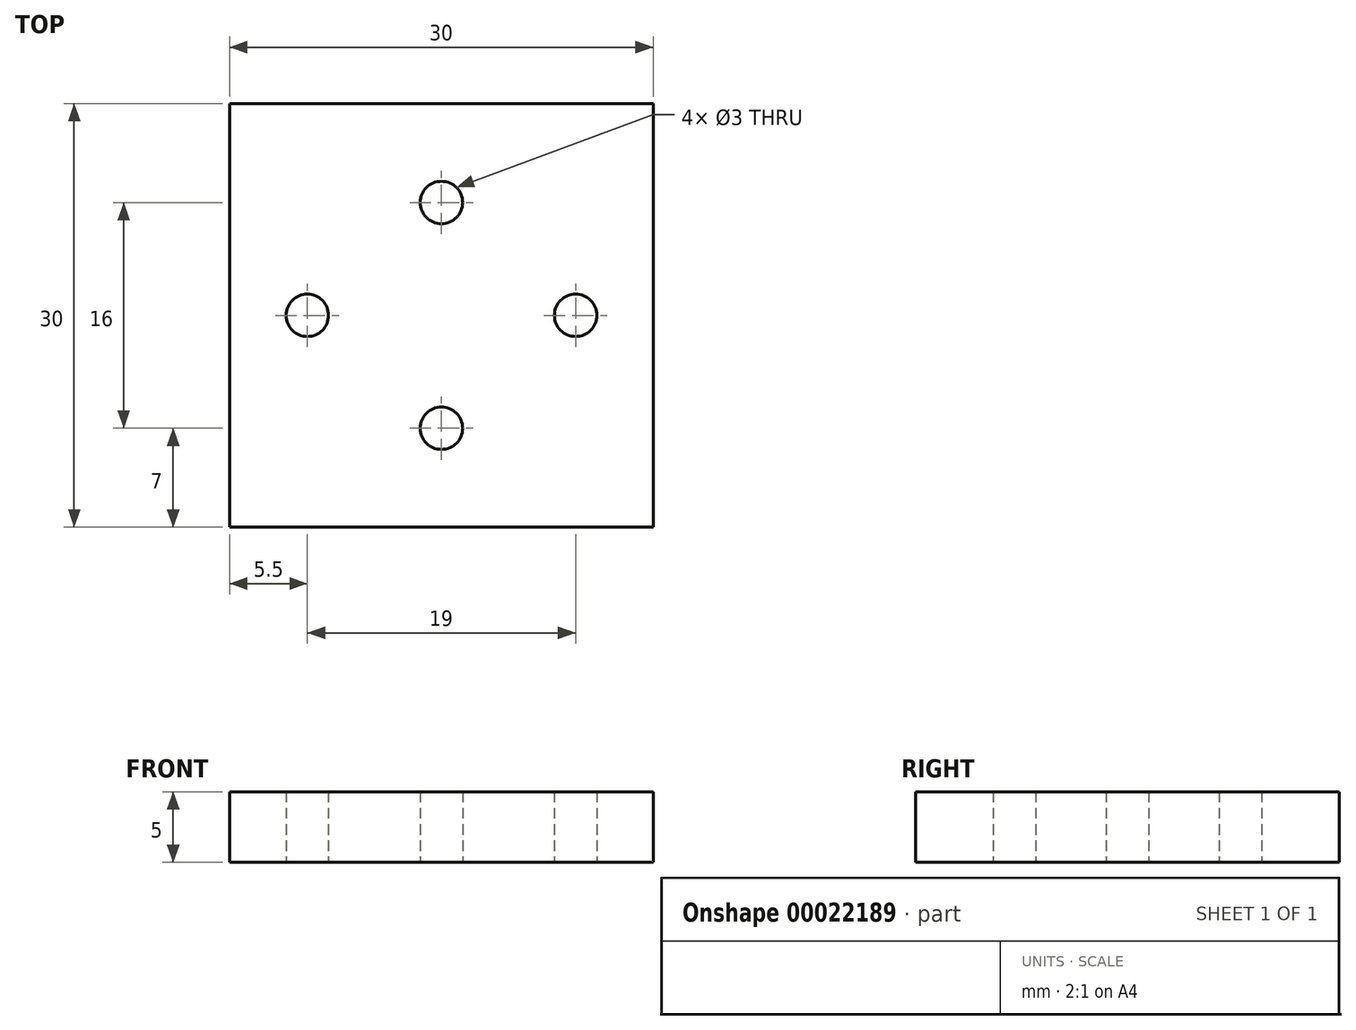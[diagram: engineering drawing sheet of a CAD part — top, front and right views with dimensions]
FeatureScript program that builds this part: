
annotation { "Feature Type Name" : "Feature", "Feature Type Description" : "" }
export const myFeature = defineFeature(function(context is Context, id is Id, definition is map)
    precondition{}
    {
        {
            var Q0;
            Q0=qCreatedBy(makeId("Top.planeOp"),FACE);
            var sketch = newSketch(context, id + "F0", { "sketchPlane" : qUnion([Q0])});
            skPoint(sketch, "E0.rect.middle", {"position": v(0, 0) * mm});
            skLineSegment(sketch, "E1", {"start": v(0, 74.97) * mm, "end": v(0, -81.59) * mm, "construction": true});
            skLineSegment(sketch, "E2", {"start": v(-74.92, 0) * mm, "end": v(75.36, 0) * mm, "construction": true});
            skLineSegment(sketch, "E3", {"start": v(0, 0) * mm, "end": v(0, 0) * mm});
            skArc(sketch, "E4.filletArc", {"start": v(-14.5, 15) * mm, "mid": v(-14.85, 14.85) * mm, "end": v(-15, 14.5) * mm});
            skArc(sketch, "E5.filletArc", {"start": v(15, 14.5) * mm, "mid": v(14.85, 14.85) * mm, "end": v(14.5, 15) * mm});
            skArc(sketch, "E6.filletArc", {"start": v(14.5, -15) * mm, "mid": v(14.85, -14.85) * mm, "end": v(15, -14.5) * mm});
            skArc(sketch, "E7.filletArc", {"start": v(-15, -14.5) * mm, "mid": v(-14.85, -14.85) * mm, "end": v(-14.5, -15) * mm});
            skCircle(sketch, "E8", {"center": v(0, 8) * mm, "radius": 1.5 * mm});
            skCircle(sketch, "E9.1.0", {"center": v(0, -8) * mm, "radius": 1.5 * mm});
            skCircle(sketch, "E10", {"center": v(-9.5, 0) * mm, "radius": 1.5 * mm});
            skCircle(sketch, "E11.1.0", {"center": v(9.5, 0) * mm, "radius": 1.5 * mm});
            skLineSegment(sketch, "E12.rect.bottom", {"start": v(15, 15) * mm, "end": v(-15, 15) * mm});
            skLineSegment(sketch, "E12.rect.top", {"start": v(15, -15) * mm, "end": v(-15, -15) * mm});
            skLineSegment(sketch, "E12.rect.left", {"start": v(15, 15) * mm, "end": v(15, -15) * mm});
            skLineSegment(sketch, "E12.rect.right", {"start": v(-15, 15) * mm, "end": v(-15, -15) * mm});
            skSolve(sketch);
        }
        {
            var Q0;
            Q0 = qSketchRegion(id + "F0", true);
            extrude(context, id + "F1", {"entities" : qUnion([Q0]), "depth" : 5 * mm});
        }
    });
